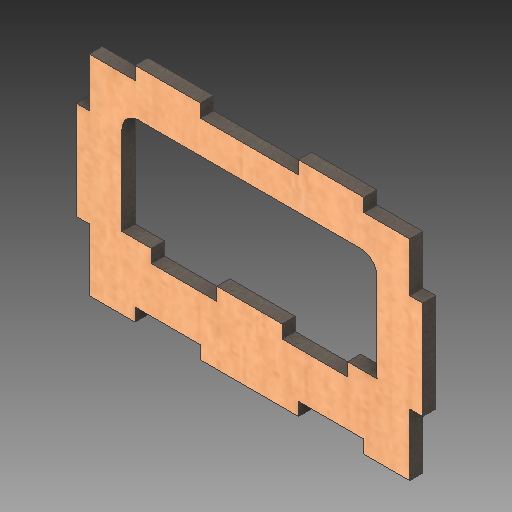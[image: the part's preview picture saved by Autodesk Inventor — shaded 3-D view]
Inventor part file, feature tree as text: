
AUTODESK INVENTOR PART (.ipt)
format: ipt  version: 2019 (Build 230136000, 136)  size: 241,152 bytes
history: native  units: mm
features: other x1, extrude x1, fillet x1
ambient origin geometry x8: Origin, YZ Plane, XZ Plane, XY Plane, X Axis, Y Axis, Z Axis, Center Point
bodies: Body1 (feature_tree)
feature tree (3):
  other  "Твердое тело1"
  extrude  "Выдавливание1"  Depth=30.0mm
  fillet  "Сопряжение1"  Radius=10.0mm
